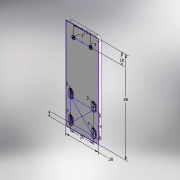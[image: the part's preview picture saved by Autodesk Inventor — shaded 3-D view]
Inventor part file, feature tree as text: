
AUTODESK INVENTOR PART (.ipt)
format: ipt  version: 2018 (Build 220112000, 112)  size: 168,960 bytes
history: native  units: mm
features: extrude x2, sketch x1, fillet x1
ambient origin geometry x8: Origin, YZ Plane, XZ Plane, XY Plane, X Axis, Y Axis, Z Axis, Center Point
bodies: Solid1 (feature_tree)
feature tree (4):
  sketch  "Sketch1"  dims[d0=75.0mm d1=28.0mm d2=20.0mm d3=20.0mm d4=4.0mm d5=5.0mm d6=3.0mm d7=5.0mm d8=3.0mm d9=5.0mm d10=3.0mm d11=5.0mm d12=3.0mm d13=3.0mm d14=0.0mm d15=3.0mm d16=3.0mm d17=3.0mm d18=15.0mm d19=10.0mm d20=3.0mm d21=0.0mm]
  extrude  "Extrusion1"  Depth=28.0mm
  fillet  "Fillet1"  Radius=20.0mm
  extrude  "Extrusion2"  Depth=20.0mm
